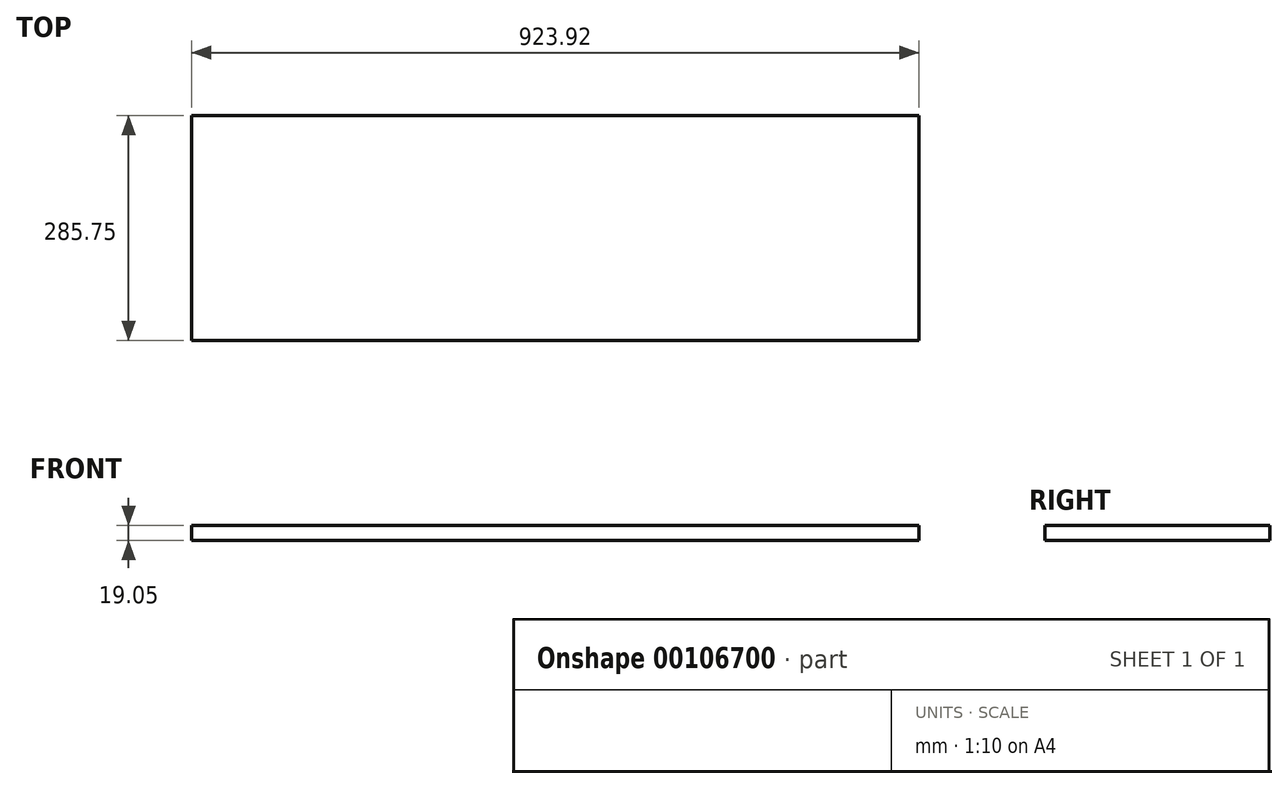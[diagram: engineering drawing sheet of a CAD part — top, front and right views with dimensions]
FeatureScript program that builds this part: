
annotation { "Feature Type Name" : "Feature", "Feature Type Description" : "" }
export const myFeature = defineFeature(function(context is Context, id is Id, definition is map)
    precondition{}
    {
        {
            var Q0;
            Q0=qCreatedBy(makeId("Top.planeOp"),FACE);
            var sketch = newSketch(context, id + "F0", { "sketchPlane" : qUnion([Q0])});
            skLineSegment(sketch, "E0.bottom", {"start": v(0, 0) * mm, "end": v(923.93, 0) * mm});
            skLineSegment(sketch, "E0.top", {"start": v(0, 285.75) * mm, "end": v(923.93, 285.75) * mm});
            skLineSegment(sketch, "E0.left", {"start": v(0, 0) * mm, "end": v(0, 285.75) * mm});
            skLineSegment(sketch, "E0.right", {"start": v(923.93, 0) * mm, "end": v(923.93, 285.75) * mm});
            skSolve(sketch);
        }
        {
            var Q0;
            Q0=makeQuery(id+"F0.imprint","IMPRINT",FACE,{"disambiguationData":[TD([[makeQuery(id+"F0.imprint","IMPRINT",EDGE,{"derivedFrom":sQuery(id+"F0.wireOp",EDGE,"E0.bottom")}),1.0]])]});
            extrude(context, id + "F1", {"entities" : qUnion([Q0]), "depth" : 19.05 * mm});
        }
    });
